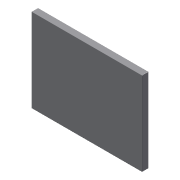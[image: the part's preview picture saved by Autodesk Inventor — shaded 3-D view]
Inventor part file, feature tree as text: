
AUTODESK INVENTOR PART (.ipt)
format: ipt  version: 2016 (Build 200138000, 138)  size: 109,568 bytes
history: native  units: mm
features: sheet_metal_op x4, sketch x2, other x2
ambient origin geometry x8: Origin, YZ Plane, XZ Plane, XY Plane, X Axis, Y Axis, Z Axis, Center Point
bodies: Solid1 (feature_tree)
feature tree (8):
  sheet_metal_op  "Face1"
  sheet_metal_op  "Flange1"
  sketch  "Sketch1"  dims[d0=700.0mm]
  other  "Plate1"
  sketch  "Sketch2"  dims[d1=529.8mm d2=0.5mm d3=0.5mm d4=0.25mm d5=1.0mm d6=0.5mm d7=40.0mm d8=90.0deg d9=0.5mm d10=2.0mm d11=0.5mm d12=0.5mm]
  other  "Plate2"
  sheet_metal_op  "Bend1"
  sheet_metal_op  "Corner1"
